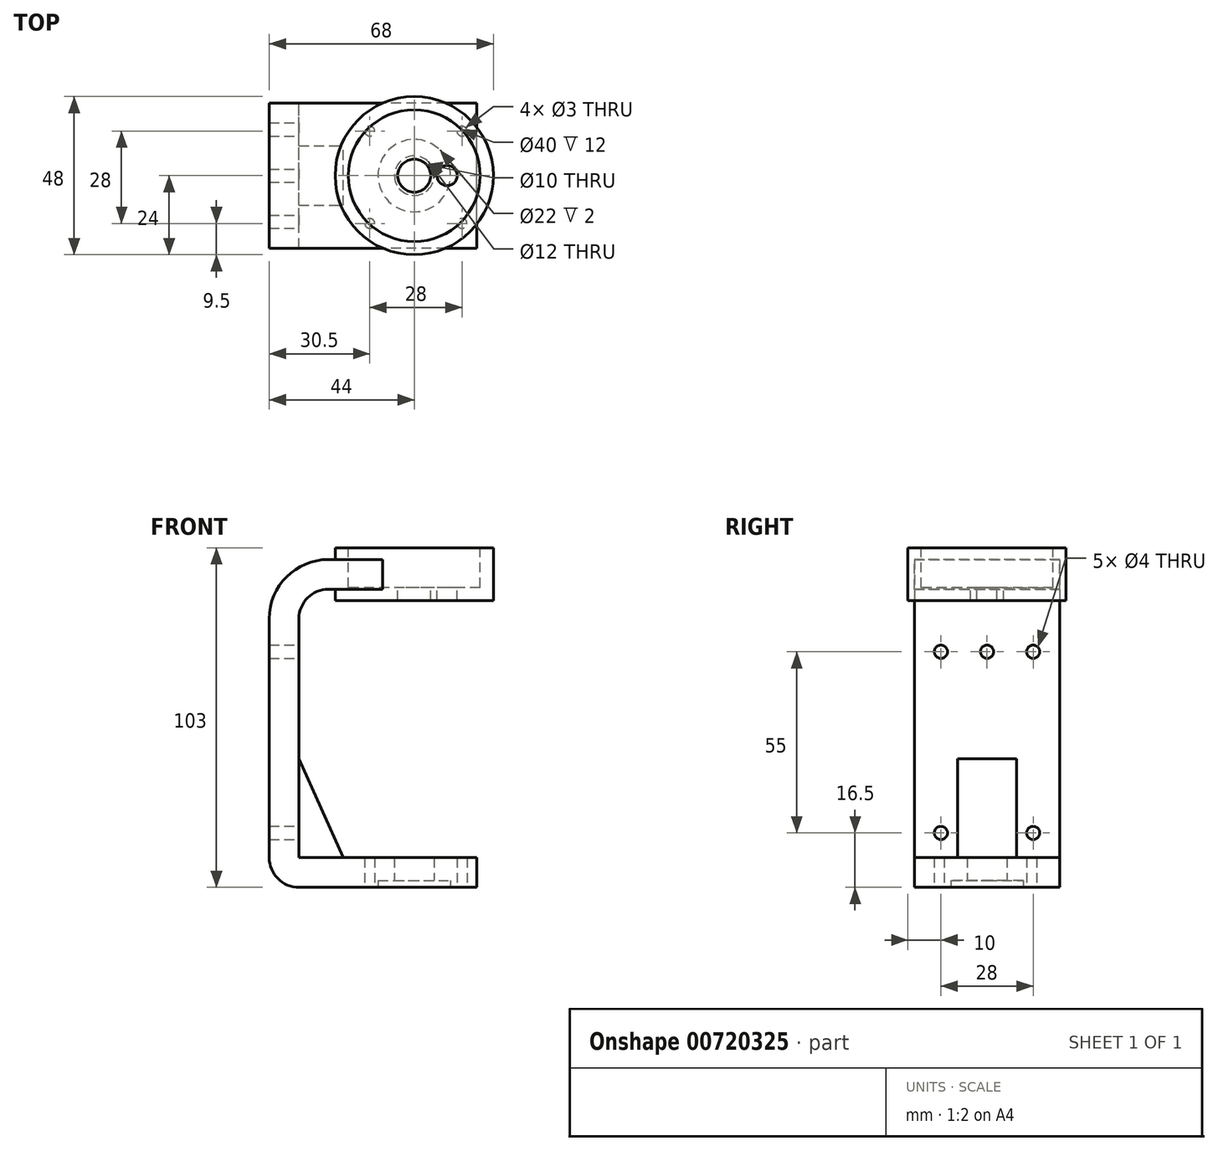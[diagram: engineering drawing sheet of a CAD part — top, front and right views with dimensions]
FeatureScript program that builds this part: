
annotation { "Feature Type Name" : "Feature", "Feature Type Description" : "" }
export const myFeature = defineFeature(function(context is Context, id is Id, definition is map)
    precondition{}
    {
        {
            var Q0;
            Q0=qCreatedBy(makeId("Front.planeOp"),FACE);
            var sketch = newSketch(context, id + "F0", { "sketchPlane" : qUnion([Q0])});
            skLineSegment(sketch, "E0.bottom", {"start": v(-14, 64) * mm, "end": v(34, 64) * mm});
            skLineSegment(sketch, "E0.top", {"start": v(-14, 48) * mm, "end": v(34, 48) * mm});
            skLineSegment(sketch, "E0.left", {"start": v(-14, 64) * mm, "end": v(-14, 48) * mm});
            skLineSegment(sketch, "E0.right", {"start": v(34, 64) * mm, "end": v(34, 48) * mm});
            skLineSegment(sketch, "E1", {"start": v(-25, 42.5) * mm, "end": v(-25, -30) * mm});
            skLineSegment(sketch, "E2", {"start": v(-25, -30) * mm, "end": v(29, -30) * mm});
            skLineSegment(sketch, "E3", {"start": v(29, -30) * mm, "end": v(29, -39) * mm});
            skLineSegment(sketch, "E4", {"start": v(29, -39) * mm, "end": v(-25, -39) * mm});
            skArc(sketch, "E5", {"start": v(-16, 51.5) * mm, "mid": v(-22.36, 48.86) * mm, "end": v(-25, 42.5) * mm});
            skLineSegment(sketch, "E6", {"start": v(-16, 51.5) * mm, "end": v(10, 51.5) * mm});
            skLineSegment(sketch, "E7.0", {"start": v(-16, 60.5) * mm, "end": v(10, 60.5) * mm});
            skArc(sketch, "E7.1", {"start": v(-16, 60.5) * mm, "mid": v(-28.73, 55.23) * mm, "end": v(-34, 42.5) * mm});
            skLineSegment(sketch, "E8.0", {"start": v(-34, 42.5) * mm, "end": v(-34, -30) * mm});
            skArc(sketch, "E9", {"start": v(-34, -30) * mm, "mid": v(-31.36, -36.36) * mm, "end": v(-25, -39) * mm});
            skLineSegment(sketch, "E10", {"start": v(-25, -30) * mm, "end": v(-25, -39) * mm});
            skLineSegment(sketch, "E11", {"start": v(10, 60.5) * mm, "end": v(10, 51.5) * mm});
            skLineSegment(sketch, "E12", {"start": v(10, 64) * mm, "end": v(10, 48) * mm});
            skLineSegment(sketch, "E13", {"start": v(-16, 51.5) * mm, "end": v(-16, 60.5) * mm});
            skLineSegment(sketch, "E14", {"start": v(10, 68.5) * mm, "end": v(10, 42.48) * mm, "construction": true});
            skPoint(sketch, "E15.oppositeSnap0", {"position": v(2, -30) * mm});
            skLineSegment(sketch, "E15.bottom", {"start": v(-25, -30) * mm, "end": v(2, -30) * mm, "construction": true});
            skLineSegment(sketch, "E15.top", {"start": v(-25, 0) * mm, "end": v(2, 0) * mm, "construction": true});
            skLineSegment(sketch, "E15.left", {"start": v(-25, -30) * mm, "end": v(-25, 0) * mm, "construction": true});
            skLineSegment(sketch, "E15.right", {"start": v(2, -30) * mm, "end": v(2, 0) * mm, "construction": true});
            skLineSegment(sketch, "E16", {"start": v(-11.5, -30) * mm, "end": v(-25, 0) * mm});
            skSolve(sketch);
        }
        {
            var Q0;
            Q0=makeQuery(id+"F0.imprint","IMPRINT",FACE,{"disambiguationData":[TD([[makeQuery(id+"F0.imprint","IMPRINT",EDGE,{"derivedFrom":sQuery(id+"F0.wireOp",EDGE,"E1")}),-1.0]])]});
            var Q1;
            Q1=makeQuery(id+"F0.imprint","IMPRINT",FACE,{"disambiguationData":[TD([[makeQuery(id+"F0.imprint","IMPRINT",EDGE,{"derivedFrom":sQuery(id+"F0.wireOp",EDGE,"E6")}),1.0]])]});
            var Q2;
            Q2=makeQuery(id+"F0.imprint","IMPRINT",FACE,{"disambiguationData":[TD([[makeQuery(id+"F0.imprint","IMPRINT",EDGE,{"derivedFrom":sQuery(id+"F0.wireOp",EDGE,"E2")}),-1.0]])]});
            extrude(context, id + "F1", {"entities" : qUnion([Q0, Q1, Q2]), "endBound" : BoundingType.SYMMETRIC, "depth" : 44 * mm, "offsetDistance" : 25 * mm});
        }
        {
            var Q0;
            {var subQ0=sQuery(id+"F0.wireOp",EDGE,"E0.right");Q0=makeQuery(id+"F0.imprint","IMPRINT",FACE,{"disambiguationData":[TD([[makeQuery(id+"F0.imprint","IMPRINT",EDGE,{"derivedFrom":subQ0}),-1.0]])]});}
            var Q1;
            Q1=sQuery(id+"F0.wireOp",EDGE,"E14");
            revolve(context, id + "F2", {"operationType" : NewBodyOperationType.ADD, "surfaceOperationType" : NewSurfaceOperationType.NEW, "entities" : qUnion([Q0]), "axis" : qUnion([Q1]), "revolveType" : RevolveType.FULL});
        }
        {
            var Q0;
            Q0=makeQuery(id+"F2.opRevolve","SWEPT_FACE",FACE,{"disambiguationData":[OSD([sQuery(id+"F0.wireOp",EDGE,"E0.bottom")])]});
            var sketch = newSketch(context, id + "F3", { "sketchPlane" : qUnion([Q0])});
            skCircle(sketch, "E17", {"center": v(10, 0) * mm, "radius": 20 * mm});
            skSolve(sketch);
        }
        {
            var Q0;
            Q0 = qSketchRegion(id + "F3", true);
            extrude(context, id + "F4", {"entities" : qUnion([Q0]), "operationType" : NewBodyOperationType.REMOVE, "oppositeDirection" : true, "depth" : 12 * mm, "offsetDistance" : 25 * mm});
        }
        {
            var Q0;
            Q0=makeQuery(id+"F4.boolean.opBoolean","COPY",FACE,{"derivedFrom":makeQuery(id+"F4.opExtrude","CAP_FACE",FACE,{"disambiguationData":[OSD([sQuery(id+"F3.wireOp",EDGE,"E17")])],"isStart":false})});
            var sketch = newSketch(context, id + "F5", { "sketchPlane" : qUnion([Q0])});
            skCircle(sketch, "E18", {"center": v(10, 0) * mm, "radius": 5 * mm});
            skCircle(sketch, "E19", {"center": v(20, 0) * mm, "radius": 3.05 * mm});
            skSolve(sketch);
        }
        {
            var Q0;
            Q0=makeQuery(id+"F5.imprint","IMPRINT",FACE,{"disambiguationData":[TD([[makeQuery(id+"F5.imprint","IMPRINT",EDGE,{"derivedFrom":sQuery(id+"F5.wireOp",EDGE,"E18")}),1.0]])]});
            var Q1;
            Q1=makeQuery(id+"F5.imprint","IMPRINT",FACE,{"disambiguationData":[TD([[makeQuery(id+"F5.imprint","IMPRINT",EDGE,{"derivedFrom":sQuery(id+"F5.wireOp",EDGE,"E19")}),1.0]])]});
            extrude(context, id + "F6", {"entities" : qUnion([Q0, Q1]), "operationType" : NewBodyOperationType.REMOVE, "oppositeDirection" : true, "depth" : 50 * mm, "offsetDistance" : 25 * mm});
        }
        {
            var Q0;
            Q0=makeQuery(id+"F1.opExtrude","SWEPT_FACE",FACE,{"disambiguationData":[OSD([sQuery(id+"F0.wireOp",EDGE,"E1")])]});
            var sketch = newSketch(context, id + "F7", { "sketchPlane" : qUnion([Q0])});
            skCircle(sketch, "E20", {"center": v(14, -22.5) * mm, "radius": 2 * mm});
            skLineSegment(sketch, "E21", {"start": v(17.15, 0) * mm, "end": v(-19.12, 0) * mm, "construction": true});
            skCircle(sketch, "E22.0.1.0", {"center": v(14, 32.5) * mm, "radius": 2 * mm});
            skCircle(sketch, "E22.1.0.0", {"center": v(0, -22.5) * mm, "radius": 2 * mm});
            skCircle(sketch, "E22.1.1.0", {"center": v(0, 32.5) * mm, "radius": 2 * mm});
            skCircle(sketch, "E22.2.0.0", {"center": v(-14, -22.5) * mm, "radius": 2 * mm});
            skCircle(sketch, "E22.2.1.0", {"center": v(-14, 32.5) * mm, "radius": 2 * mm});
            skLineSegment(sketch, "E22.direction1", {"start": v(14, -22.5) * mm, "end": v(0, -22.5) * mm, "construction": true});
            skLineSegment(sketch, "E22.direction2", {"start": v(14, -22.5) * mm, "end": v(14, 32.5) * mm, "construction": true});
            skSolve(sketch);
        }
        {
            var Q0;
            Q0=makeQuery(id+"F7.imprint","IMPRINT",FACE,{"disambiguationData":[TD([[makeQuery(id+"F7.imprint","IMPRINT",EDGE,{"derivedFrom":sQuery(id+"F7.wireOp",EDGE,"E20")}),1.0]])]});
            var Q1;
            Q1=makeQuery(id+"F7.imprint","IMPRINT",FACE,{"disambiguationData":[TD([[makeQuery(id+"F7.imprint","IMPRINT",EDGE,{"derivedFrom":sQuery(id+"F7.wireOp",EDGE,"E22.0.1.0")}),1.0]])]});
            var Q2;
            Q2=makeQuery(id+"F7.imprint","IMPRINT",FACE,{"disambiguationData":[TD([[makeQuery(id+"F7.imprint","IMPRINT",EDGE,{"derivedFrom":sQuery(id+"F7.wireOp",EDGE,"E22.1.1.0")}),1.0]])]});
            var Q3;
            Q3=makeQuery(id+"F7.imprint","IMPRINT",FACE,{"disambiguationData":[TD([[makeQuery(id+"F7.imprint","IMPRINT",EDGE,{"derivedFrom":sQuery(id+"F7.wireOp",EDGE,"E22.2.0.0")}),1.0]])]});
            var Q4;
            Q4=makeQuery(id+"F7.imprint","IMPRINT",FACE,{"disambiguationData":[TD([[makeQuery(id+"F7.imprint","IMPRINT",EDGE,{"derivedFrom":sQuery(id+"F7.wireOp",EDGE,"E22.2.1.0")}),1.0]])]});
            extrude(context, id + "F8", {"entities" : qUnion([Q0, Q1, Q2, Q3, Q4]), "operationType" : NewBodyOperationType.REMOVE, "endBound" : BoundingType.THROUGH_ALL, "oppositeDirection" : true, "depth" : 25 * mm, "offsetDistance" : 25 * mm});
        }
        {
            var Q0;
            Q0=makeQuery(id+"F1.opExtrude","SWEPT_FACE",FACE,{"disambiguationData":[OSD([sQuery(id+"F0.wireOp",EDGE,"E4")])]});
            var sketch = newSketch(context, id + "F9", { "sketchPlane" : qUnion([Q0])});
            skCircle(sketch, "E23", {"center": v(10, 0) * mm, "radius": 11 * mm});
            skSolve(sketch);
        }
        {
            var Q0;
            Q0 = qSketchRegion(id + "F9", true);
            extrude(context, id + "F10", {"entities" : qUnion([Q0]), "operationType" : NewBodyOperationType.REMOVE, "oppositeDirection" : true, "depth" : 2 * mm, "offsetDistance" : 25 * mm});
        }
        {
            var Q0;
            Q0=makeQuery(id+"F1.opExtrude","SWEPT_FACE",FACE,{"disambiguationData":[OSD([sQuery(id+"F0.wireOp",EDGE,"E4")])]});
            var sketch = newSketch(context, id + "F11", { "sketchPlane" : qUnion([Q0])});
            skCircle(sketch, "E24", {"center": v(-3.5, -13.5) * mm, "radius": 1.5 * mm});
            skCircle(sketch, "E25.0.1.0", {"center": v(-3.5, 14.5) * mm, "radius": 1.5 * mm});
            skCircle(sketch, "E25.1.0.0", {"center": v(24.5, -13.5) * mm, "radius": 1.5 * mm});
            skCircle(sketch, "E25.1.1.0", {"center": v(24.5, 14.5) * mm, "radius": 1.5 * mm});
            skCircle(sketch, "E25.2.0.0", {"center": v(52.5, -13.5) * mm, "radius": 1.5 * mm});
            skCircle(sketch, "E25.2.1.0", {"center": v(52.5, 14.5) * mm, "radius": 1.5 * mm});
            skLineSegment(sketch, "E25.direction1", {"start": v(-3.5, -13.5) * mm, "end": v(24.5, -13.5) * mm, "construction": true});
            skLineSegment(sketch, "E25.direction2", {"start": v(-3.5, -13.5) * mm, "end": v(-3.5, 14.5) * mm, "construction": true});
            skSolve(sketch);
        }
        {
            var Q0;
            Q0 = qSketchRegion(id + "F11", true);
            extrude(context, id + "F12", {"entities" : qUnion([Q0]), "operationType" : NewBodyOperationType.REMOVE, "oppositeDirection" : true, "depth" : 20 * mm, "offsetDistance" : 25 * mm});
        }
        {
            var Q0;
            Q0=makeQuery(id+"F1.opExtrude","SWEPT_FACE",FACE,{"disambiguationData":[OSD([sQuery(id+"F0.wireOp",EDGE,"E4")])]});
            var sketch = newSketch(context, id + "F13", { "sketchPlane" : qUnion([Q0])});
            skCircle(sketch, "E26", {"center": v(10, 0) * mm, "radius": 6 * mm});
            skSolve(sketch);
        }
        {
            var Q0;
            Q0=makeQuery(id+"F13.imprint","IMPRINT",FACE,{"disambiguationData":[TD([[makeQuery(id+"F13.imprint","IMPRINT",EDGE,{"derivedFrom":sQuery(id+"F13.wireOp",EDGE,"E26")}),1.0]])]});
            extrude(context, id + "F14", {"entities" : qUnion([Q0]), "operationType" : NewBodyOperationType.REMOVE, "oppositeDirection" : true, "depth" : 25 * mm, "offsetDistance" : 25 * mm});
        }
        {
            var Q0;
            {var subQ3=sQuery(id+"F0.wireOp",EDGE,"E16");Q0=makeQuery(id+"F0.imprint","IMPRINT",FACE,{"disambiguationData":[TD([[makeQuery(id+"F0.imprint","IMPRINT",EDGE,{"derivedFrom":subQ3}),1.0]])]});}
            extrude(context, id + "F15", {"entities" : qUnion([Q0]), "operationType" : NewBodyOperationType.ADD, "endBound" : BoundingType.SYMMETRIC, "depth" : 18 * mm, "offsetDistance" : 25 * mm});
        }
    });
